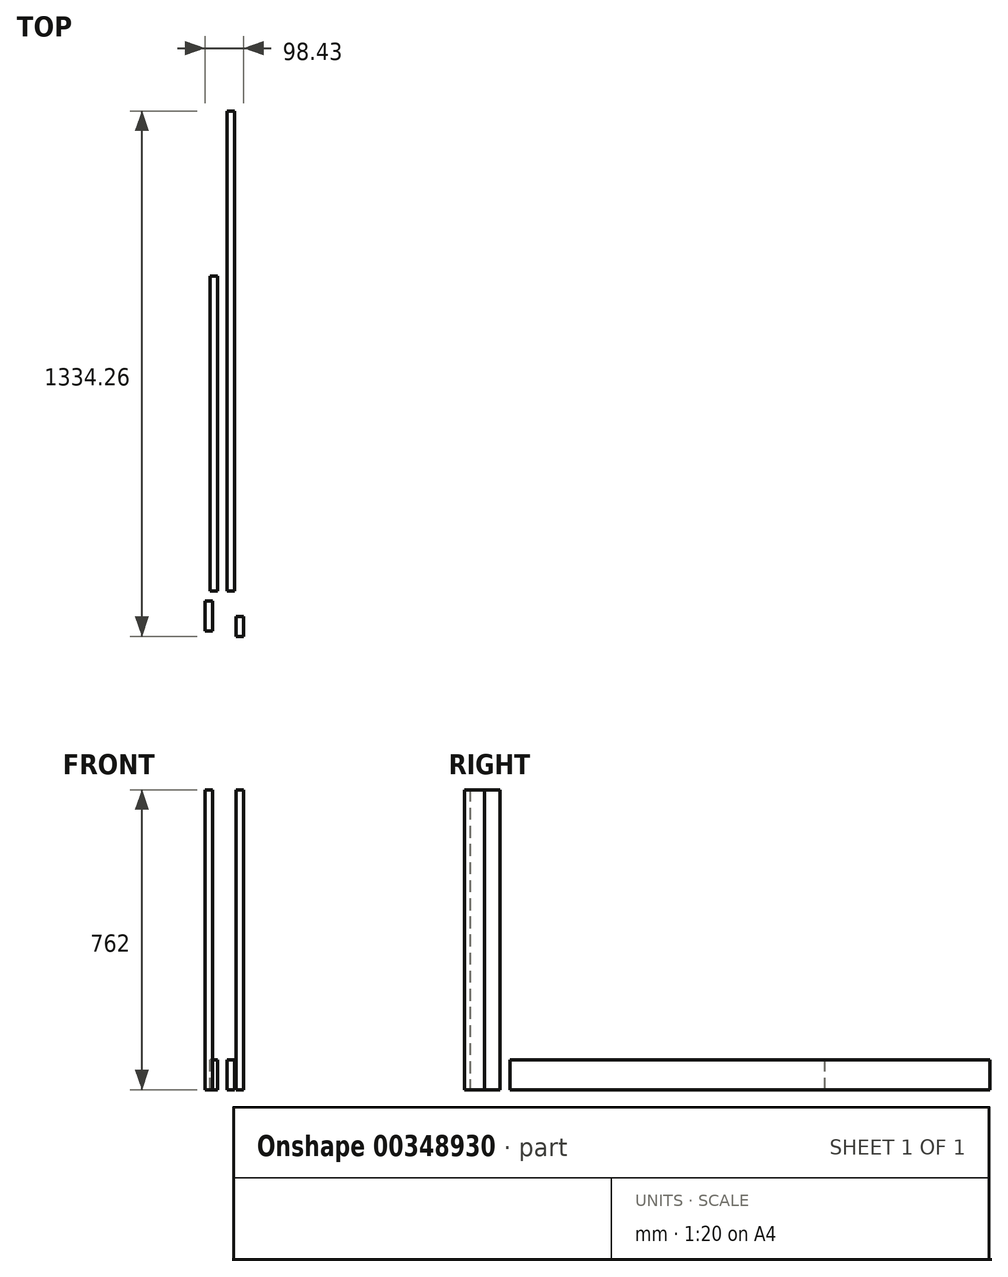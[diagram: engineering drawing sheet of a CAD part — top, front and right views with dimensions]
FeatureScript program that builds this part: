
annotation { "Feature Type Name" : "Feature", "Feature Type Description" : "" }
export const myFeature = defineFeature(function(context is Context, id is Id, definition is map)
    precondition{}
    {
        {
            var Q0;
            Q0=qCreatedBy(makeId("Front.planeOp"),FACE);
            var sketch = newSketch(context, id + "F0", { "sketchPlane" : qUnion([Q0])});
            skLineSegment(sketch, "E0.bottom", {"start": v(0, 0) * mm, "end": v(19.05, 0) * mm});
            skLineSegment(sketch, "E0.top", {"start": v(0, 76.2) * mm, "end": v(19.05, 76.2) * mm});
            skLineSegment(sketch, "E0.left", {"start": v(0, 0) * mm, "end": v(0, 76.2) * mm});
            skLineSegment(sketch, "E0.right", {"start": v(19.05, 0) * mm, "end": v(19.05, 76.2) * mm});
            skSolve(sketch);
        }
        {
            var Q0;
            Q0=makeQuery(id+"F0.imprint","IMPRINT",FACE,{"disambiguationData":[TD([[makeQuery(id+"F0.imprint","IMPRINT",EDGE,{"derivedFrom":sQuery(id+"F0.wireOp",EDGE,"E0.bottom")}),1.0]])]});
            extrude(context, id + "F1", {"entities" : qUnion([Q0]), "oppositeDirection" : true, "depth" : 1219.2 * mm});
        }
        {
            var Q0;
            Q0=qCreatedBy(makeId("Front.planeOp"),FACE);
            var sketch = newSketch(context, id + "F2", { "sketchPlane" : qUnion([Q0])});
            skLineSegment(sketch, "E1.bottom", {"start": v(-25.02, 0) * mm, "end": v(-44.07, 0) * mm});
            skLineSegment(sketch, "E1.top", {"start": v(-25.02, 76.2) * mm, "end": v(-44.07, 76.2) * mm});
            skLineSegment(sketch, "E1.left", {"start": v(-25.02, 0) * mm, "end": v(-25.02, 76.2) * mm});
            skLineSegment(sketch, "E1.right", {"start": v(-44.07, 0) * mm, "end": v(-44.07, 76.2) * mm});
            skSolve(sketch);
        }
        {
            var Q0;
            Q0=makeQuery(id+"F2.imprint","IMPRINT",FACE,{"disambiguationData":[TD([[makeQuery(id+"F2.imprint","IMPRINT",EDGE,{"derivedFrom":sQuery(id+"F2.wireOp",EDGE,"E1.bottom")}),-1.0]])]});
            extrude(context, id + "F3", {"entities" : qUnion([Q0]), "oppositeDirection" : true, "depth" : 800.1 * mm});
        }
        {
            var Q0;
            Q0=qCreatedBy(makeId("Top.planeOp"),FACE);
            var sketch = newSketch(context, id + "F4", { "sketchPlane" : qUnion([Q0])});
            skLineSegment(sketch, "E2.bottom", {"start": v(-56.87, -25.4) * mm, "end": v(-37.82, -25.4) * mm});
            skLineSegment(sketch, "E2.top", {"start": v(-56.87, -101.6) * mm, "end": v(-37.82, -101.6) * mm});
            skLineSegment(sketch, "E2.left", {"start": v(-56.87, -25.4) * mm, "end": v(-56.87, -101.6) * mm});
            skLineSegment(sketch, "E2.right", {"start": v(-37.82, -25.4) * mm, "end": v(-37.82, -101.6) * mm});
            skSolve(sketch);
        }
        {
            var Q0;
            Q0=makeQuery(id+"F4.imprint","IMPRINT",FACE,{"disambiguationData":[TD([[makeQuery(id+"F4.imprint","IMPRINT",EDGE,{"derivedFrom":sQuery(id+"F4.wireOp",EDGE,"E2.bottom")}),-1.0]])]});
            extrude(context, id + "F5", {"entities" : qUnion([Q0]), "depth" : 762 * mm});
        }
        {
            var Q0;
            Q0=qCreatedBy(makeId("Top.planeOp"),FACE);
            var sketch = newSketch(context, id + "F6", { "sketchPlane" : qUnion([Q0])});
            skLineSegment(sketch, "E3.bottom", {"start": v(22.5, -64.26) * mm, "end": v(41.56, -64.26) * mm});
            skLineSegment(sketch, "E3.top", {"start": v(22.5, -115.06) * mm, "end": v(41.56, -115.06) * mm});
            skLineSegment(sketch, "E3.left", {"start": v(22.5, -64.26) * mm, "end": v(22.5, -115.06) * mm});
            skLineSegment(sketch, "E3.right", {"start": v(41.56, -64.26) * mm, "end": v(41.56, -115.06) * mm});
            skSolve(sketch);
        }
        {
            var Q0;
            Q0=makeQuery(id+"F6.imprint","IMPRINT",FACE,{"disambiguationData":[TD([[makeQuery(id+"F6.imprint","IMPRINT",EDGE,{"derivedFrom":sQuery(id+"F6.wireOp",EDGE,"E3.bottom")}),-1.0]])]});
            extrude(context, id + "F7", {"entities" : qUnion([Q0]), "depth" : 762 * mm});
        }
    });
